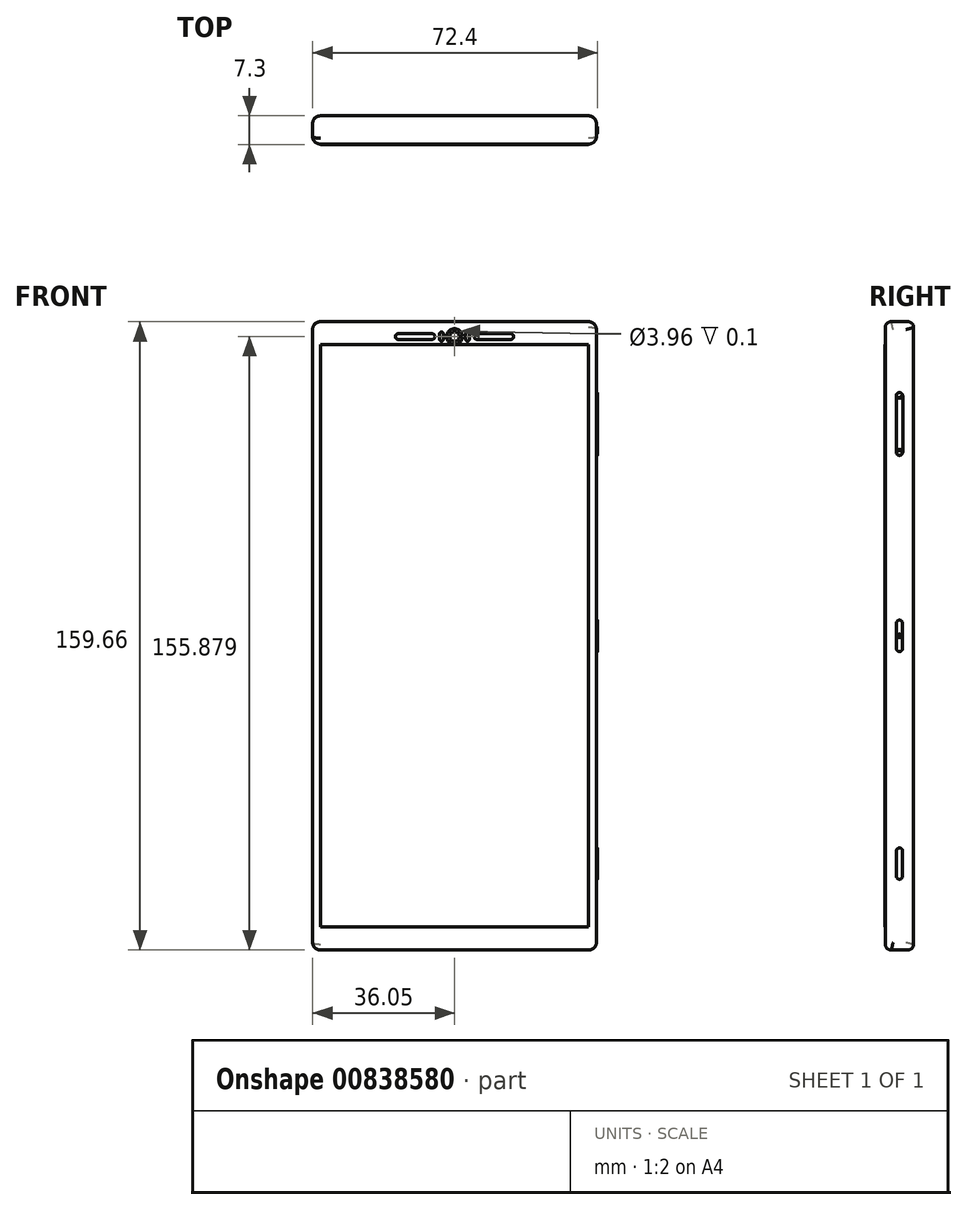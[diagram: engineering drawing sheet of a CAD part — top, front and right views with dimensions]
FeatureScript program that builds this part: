
annotation { "Feature Type Name" : "Feature", "Feature Type Description" : "" }
export const myFeature = defineFeature(function(context is Context, id is Id, definition is map)
    precondition{}
    {
        {
            var Q0;
            Q0=qCreatedBy(makeId("Front.planeOp"),FACE);
            var sketch = newSketch(context, id + "F0", { "sketchPlane" : qUnion([Q0])});
            skLineSegment(sketch, "E0.bottom", {"start": v(36.05, -79.83) * mm, "end": v(-36.05, -79.83) * mm});
            skLineSegment(sketch, "E0.top", {"start": v(36.05, 79.83) * mm, "end": v(-36.05, 79.83) * mm});
            skLineSegment(sketch, "E0.left", {"start": v(36.05, -79.83) * mm, "end": v(36.05, 79.83) * mm});
            skLineSegment(sketch, "E0.right", {"start": v(-36.05, -79.83) * mm, "end": v(-36.05, 79.83) * mm});
            skPoint(sketch, "E0.middle", {"position": v(0, 0) * mm});
            skSolve(sketch);
        }
        {
            var Q0;
            Q0=makeQuery(id+"F0.imprint","IMPRINT",FACE,{"disambiguationData":[TD([[makeQuery(id+"F0.imprint","IMPRINT",EDGE,{"derivedFrom":sQuery(id+"F0.wireOp",EDGE,"E0.bottom")}),-1.0]])]});
            extrude(context, id + "F1", {"entities" : qUnion([Q0]), "depth" : 7.2 * mm, "offsetDistance" : 25 * mm});
        }
        {
            var Q0;
            Q0=makeQuery(id+"F1.opExtrude","CAP_EDGE",EDGE,{"disambiguationData":[OSD([sQuery(id+"F0.wireOp",EDGE,"E0.bottom")])],"isStart":false});
            var Q1;
            Q1=makeQuery(id+"F1.opExtrude","CAP_EDGE",EDGE,{"disambiguationData":[OSD([sQuery(id+"F0.wireOp",EDGE,"E0.bottom")])],"isStart":true});
            var Q2;
            Q2=makeQuery(id+"F1.opExtrude","CAP_EDGE",EDGE,{"disambiguationData":[OSD([sQuery(id+"F0.wireOp",EDGE,"E0.top")])],"isStart":false});
            var Q3;
            Q3=makeQuery(id+"F1.opExtrude","CAP_EDGE",EDGE,{"disambiguationData":[OSD([sQuery(id+"F0.wireOp",EDGE,"E0.top")])],"isStart":true});
            fillet(context, id + "F2", {"entities" : qUnion([Q0, Q1, Q2, Q3]), "radius" : 1.5 * mm, "tangentPropagation" : true, "allowEdgeOverflow" : false});
        }
        {
            var Q0;
            Q0=makeQuery(id+"F1.opExtrude","CAP_EDGE",EDGE,{"disambiguationData":[OSD([sQuery(id+"F0.wireOp",EDGE,"E0.right")])],"isStart":false});
            var Q1;
            Q1=makeQuery(id+"F1.opExtrude","CAP_EDGE",EDGE,{"disambiguationData":[OSD([sQuery(id+"F0.wireOp",EDGE,"E0.left")])],"isStart":false});
            fillet(context, id + "F3", {"entities" : qUnion([Q0, Q1]), "radius" : 2 * mm, "tangentPropagation" : true, "allowEdgeOverflow" : false});
        }
        {
            var Q0;
            Q0=makeQuery(id+"F1.opExtrude","CAP_FACE",FACE,{"disambiguationData":[OSD([sQuery(id+"F0.wireOp",EDGE,"E0.bottom"),sQuery(id+"F0.wireOp",EDGE,"E0.top"),sQuery(id+"F0.wireOp",EDGE,"E0.left"),sQuery(id+"F0.wireOp",EDGE,"E0.right")])],"isStart":false});
            var sketch = newSketch(context, id + "F4", { "sketchPlane" : qUnion([Q0])});
            skLineSegment(sketch, "E1.bottom", {"start": v(34.05, -74) * mm, "end": v(-34.05, -74) * mm});
            skLineSegment(sketch, "E1.top", {"start": v(34.05, 74) * mm, "end": v(-34.05, 74) * mm});
            skLineSegment(sketch, "E1.left", {"start": v(34.05, -74) * mm, "end": v(34.05, 74) * mm});
            skLineSegment(sketch, "E1.right", {"start": v(-34.05, -74) * mm, "end": v(-34.05, 74) * mm});
            skPoint(sketch, "E1.middle", {"position": v(0, 0) * mm});
            skSolve(sketch);
        }
        {
            var Q0;
            {var subQ0=sQuery(id+"F4.wireOp",EDGE,"E1.top");Q0=makeQuery(id+"F4.imprint","IMPRINT",FACE,{"disambiguationData":[TD([[makeQuery(id+"F4.imprint","IMPRINT",EDGE,{"derivedFrom":subQ0}),-1.0]])]});}
            var sketch = newSketch(context, id + "F5", { "sketchPlane" : qUnion([Q0])});
            skCircle(sketch, "E2", {"center": v(0, 76.05) * mm, "radius": 1.98 * mm});
            skCircle(sketch, "E3", {"center": v(0, 76.05) * mm, "radius": 1.22 * mm});
            skLineSegment(sketch, "E4.bottom", {"start": v(15.02, 75.32) * mm, "end": v(5, 75.32) * mm});
            skLineSegment(sketch, "E4.top", {"start": v(15.02, 76.77) * mm, "end": v(5, 76.77) * mm});
            skLineSegment(sketch, "E4.left", {"start": v(15.02, 75.32) * mm, "end": v(15.02, 76.77) * mm});
            skLineSegment(sketch, "E4.right", {"start": v(5, 75.32) * mm, "end": v(5, 76.77) * mm});
            skLineSegment(sketch, "E5.bottom", {"start": v(-4.99, 75.32) * mm, "end": v(-15.03, 75.32) * mm});
            skLineSegment(sketch, "E5.top", {"start": v(-4.99, 76.77) * mm, "end": v(-15.03, 76.77) * mm});
            skLineSegment(sketch, "E5.left", {"start": v(-4.99, 75.32) * mm, "end": v(-4.99, 76.77) * mm});
            skLineSegment(sketch, "E5.right", {"start": v(-15.03, 75.32) * mm, "end": v(-15.03, 76.77) * mm});
            skLineSegment(sketch, "E6.bottom", {"start": v(3.8, 74.84) * mm, "end": v(2.83, 74.84) * mm});
            skLineSegment(sketch, "E6.top", {"start": v(3.8, 77.26) * mm, "end": v(2.83, 77.26) * mm});
            skLineSegment(sketch, "E6.left", {"start": v(3.8, 74.84) * mm, "end": v(3.8, 77.26) * mm});
            skLineSegment(sketch, "E6.right", {"start": v(2.83, 74.84) * mm, "end": v(2.83, 77.26) * mm});
            skLineSegment(sketch, "E7.bottom", {"start": v(-2.83, 74.84) * mm, "end": v(-3.8, 74.84) * mm});
            skLineSegment(sketch, "E7.top", {"start": v(-2.83, 77.26) * mm, "end": v(-3.8, 77.26) * mm});
            skLineSegment(sketch, "E7.left", {"start": v(-2.83, 74.84) * mm, "end": v(-2.83, 77.26) * mm});
            skLineSegment(sketch, "E7.right", {"start": v(-3.8, 74.84) * mm, "end": v(-3.8, 77.26) * mm});
            skSolve(sketch);
        }
        {
            var Q0;
            Q0=makeQuery(id+"F5.imprint","IMPRINT",FACE,{"disambiguationData":[TD([[makeQuery(id+"F5.imprint","IMPRINT",EDGE,{"derivedFrom":sQuery(id+"F5.wireOp",EDGE,"E5.bottom")}),-1.0]])]});
            var Q1;
            Q1=makeQuery(id+"F5.imprint","IMPRINT",FACE,{"disambiguationData":[TD([[makeQuery(id+"F5.imprint","IMPRINT",EDGE,{"derivedFrom":sQuery(id+"F5.wireOp",EDGE,"E4.bottom")}),-1.0]])]});
            var Q2;
            Q2=makeQuery(id+"F5.imprint","IMPRINT",FACE,{"disambiguationData":[TD([[makeQuery(id+"F5.imprint","IMPRINT",EDGE,{"derivedFrom":sQuery(id+"F5.wireOp",EDGE,"E6.bottom")}),-1.0]])]});
            var Q3;
            Q3=makeQuery(id+"F5.imprint","IMPRINT",FACE,{"disambiguationData":[TD([[makeQuery(id+"F5.imprint","IMPRINT",EDGE,{"derivedFrom":sQuery(id+"F5.wireOp",EDGE,"E7.bottom")}),-1.0]])]});
            var Q4;
            Q4=makeQuery(id+"F5.imprint","IMPRINT",FACE,{"disambiguationData":[TD([[makeQuery(id+"F5.imprint","IMPRINT",EDGE,{"derivedFrom":sQuery(id+"F5.wireOp",EDGE,"E2")}),1.0]])]});
            var Q5;
            Q5=sQuery(id+"F5.wireOp",EDGE,"E5.right");
            var Q6;
            Q6=sQuery(id+"F5.wireOp",EDGE,"E5.top");
            var Q7;
            Q7=sQuery(id+"F5.wireOp",EDGE,"E5.bottom");
            var Q8;
            Q8=sQuery(id+"F5.wireOp",EDGE,"E5.left");
            var Q9;
            Q9=sQuery(id+"F5.wireOp",EDGE,"E4.top");
            var Q10;
            Q10=sQuery(id+"F5.wireOp",EDGE,"E4.bottom");
            var Q11;
            Q11=sQuery(id+"F5.wireOp",EDGE,"E4.right");
            var Q12;
            Q12=sQuery(id+"F5.wireOp",EDGE,"E4.left");
            var Q13;
            Q13=sQuery(id+"F5.wireOp",EDGE,"E7.right");
            var Q14;
            Q14=sQuery(id+"F5.wireOp",EDGE,"E7.top");
            var Q15;
            Q15=sQuery(id+"F5.wireOp",EDGE,"E7.left");
            var Q16;
            Q16=sQuery(id+"F5.wireOp",EDGE,"E7.bottom");
            var Q17;
            Q17=sQuery(id+"F5.wireOp",EDGE,"E2");
            var Q18;
            Q18=sQuery(id+"F5.wireOp",EDGE,"E3");
            var Q19;
            Q19=sQuery(id+"F5.wireOp",EDGE,"E6.right");
            var Q20;
            Q20=sQuery(id+"F5.wireOp",EDGE,"E6.top");
            var Q21;
            Q21=sQuery(id+"F5.wireOp",EDGE,"E6.left");
            var Q22;
            Q22=sQuery(id+"F5.wireOp",EDGE,"E6.bottom");
            extrude(context, id + "F6", {"entities" : qUnion([Q0, Q1, Q2, Q3, Q4]), "operationType" : NewBodyOperationType.REMOVE, "surfaceEntities" : qUnion([Q5, Q6, Q7, Q8, Q9, Q10, Q11, Q12, Q13, Q14, Q15, Q16, Q17, Q18, Q19, Q20, Q21, Q22]), "oppositeDirection" : true, "depth" : .1 * mm, "offsetDistance" : 25 * mm});
        }
        {
            var Q0;
            Q0=makeQuery(id+"F6.boolean.opBoolean","COPY",EDGE,{"derivedFrom":makeQuery(id+"F6.opExtrude","SWEPT_EDGE",EDGE,{"disambiguationData":[OSD([sQuery(id+"F5.wireOp",EDGE,"E5.bottom"),sQuery(id+"F5.wireOp",EDGE,"E5.left")])]})});
            var Q1;
            Q1=makeQuery(id+"F6.boolean.opBoolean","COPY",EDGE,{"derivedFrom":makeQuery(id+"F6.opExtrude","SWEPT_EDGE",EDGE,{"disambiguationData":[OSD([sQuery(id+"F5.wireOp",EDGE,"E5.top"),sQuery(id+"F5.wireOp",EDGE,"E5.left")])]})});
            var Q2;
            Q2=makeQuery(id+"F6.boolean.opBoolean","COPY",EDGE,{"derivedFrom":makeQuery(id+"F6.opExtrude","SWEPT_EDGE",EDGE,{"disambiguationData":[OSD([sQuery(id+"F5.wireOp",EDGE,"E5.bottom"),sQuery(id+"F5.wireOp",EDGE,"E5.right")])]})});
            var Q3;
            Q3=makeQuery(id+"F6.boolean.opBoolean","COPY",EDGE,{"derivedFrom":makeQuery(id+"F6.opExtrude","SWEPT_EDGE",EDGE,{"disambiguationData":[OSD([sQuery(id+"F5.wireOp",EDGE,"E5.top"),sQuery(id+"F5.wireOp",EDGE,"E5.right")])]})});
            var Q4;
            Q4=makeQuery(id+"F6.boolean.opBoolean","COPY",EDGE,{"derivedFrom":makeQuery(id+"F6.opExtrude","SWEPT_EDGE",EDGE,{"disambiguationData":[OSD([sQuery(id+"F5.wireOp",EDGE,"E4.bottom"),sQuery(id+"F5.wireOp",EDGE,"E4.right")])]})});
            var Q5;
            Q5=makeQuery(id+"F6.boolean.opBoolean","COPY",EDGE,{"derivedFrom":makeQuery(id+"F6.opExtrude","SWEPT_EDGE",EDGE,{"disambiguationData":[OSD([sQuery(id+"F5.wireOp",EDGE,"E4.top"),sQuery(id+"F5.wireOp",EDGE,"E4.right")])]})});
            var Q6;
            Q6=makeQuery(id+"F6.boolean.opBoolean","COPY",EDGE,{"derivedFrom":makeQuery(id+"F6.opExtrude","SWEPT_EDGE",EDGE,{"disambiguationData":[OSD([sQuery(id+"F5.wireOp",EDGE,"E4.bottom"),sQuery(id+"F5.wireOp",EDGE,"E4.left")])]})});
            var Q7;
            Q7=makeQuery(id+"F6.boolean.opBoolean","COPY",EDGE,{"derivedFrom":makeQuery(id+"F6.opExtrude","SWEPT_EDGE",EDGE,{"disambiguationData":[OSD([sQuery(id+"F5.wireOp",EDGE,"E4.top"),sQuery(id+"F5.wireOp",EDGE,"E4.left")])]})});
            fillet(context, id + "F7", {"entities" : qUnion([Q0, Q1, Q2, Q3, Q4, Q5, Q6, Q7]), "radius" : .7 * mm, "tangentPropagation" : true, "allowEdgeOverflow" : false});
        }
        {
            var Q0;
            Q0=makeQuery(id+"F6.boolean.opBoolean","COPY",EDGE,{"derivedFrom":makeQuery(id+"F6.opExtrude","SWEPT_EDGE",EDGE,{"disambiguationData":[OSD([sQuery(id+"F5.wireOp",EDGE,"E7.bottom"),sQuery(id+"F5.wireOp",EDGE,"E7.left")])]})});
            var Q1;
            Q1=makeQuery(id+"F6.boolean.opBoolean","COPY",EDGE,{"derivedFrom":makeQuery(id+"F6.opExtrude","SWEPT_EDGE",EDGE,{"disambiguationData":[OSD([sQuery(id+"F5.wireOp",EDGE,"E7.bottom"),sQuery(id+"F5.wireOp",EDGE,"E7.right")])]})});
            var Q2;
            Q2=makeQuery(id+"F6.boolean.opBoolean","COPY",EDGE,{"derivedFrom":makeQuery(id+"F6.opExtrude","SWEPT_EDGE",EDGE,{"disambiguationData":[OSD([sQuery(id+"F5.wireOp",EDGE,"E7.top"),sQuery(id+"F5.wireOp",EDGE,"E7.right")])]})});
            var Q3;
            Q3=makeQuery(id+"F6.boolean.opBoolean","COPY",EDGE,{"derivedFrom":makeQuery(id+"F6.opExtrude","SWEPT_EDGE",EDGE,{"disambiguationData":[OSD([sQuery(id+"F5.wireOp",EDGE,"E7.top"),sQuery(id+"F5.wireOp",EDGE,"E7.left")])]})});
            var Q4;
            Q4=makeQuery(id+"F6.boolean.opBoolean","COPY",EDGE,{"derivedFrom":makeQuery(id+"F6.opExtrude","SWEPT_EDGE",EDGE,{"disambiguationData":[OSD([sQuery(id+"F5.wireOp",EDGE,"E6.top"),sQuery(id+"F5.wireOp",EDGE,"E6.left")])]})});
            var Q5;
            Q5=makeQuery(id+"F6.boolean.opBoolean","COPY",EDGE,{"derivedFrom":makeQuery(id+"F6.opExtrude","SWEPT_EDGE",EDGE,{"disambiguationData":[OSD([sQuery(id+"F5.wireOp",EDGE,"E6.bottom"),sQuery(id+"F5.wireOp",EDGE,"E6.left")])]})});
            var Q6;
            Q6=makeQuery(id+"F6.boolean.opBoolean","COPY",EDGE,{"derivedFrom":makeQuery(id+"F6.opExtrude","SWEPT_EDGE",EDGE,{"disambiguationData":[OSD([sQuery(id+"F5.wireOp",EDGE,"E6.bottom"),sQuery(id+"F5.wireOp",EDGE,"E6.right")])]})});
            var Q7;
            Q7=makeQuery(id+"F6.boolean.opBoolean","COPY",EDGE,{"derivedFrom":makeQuery(id+"F6.opExtrude","SWEPT_EDGE",EDGE,{"disambiguationData":[OSD([sQuery(id+"F5.wireOp",EDGE,"E6.top"),sQuery(id+"F5.wireOp",EDGE,"E6.right")])]})});
            fillet(context, id + "F8", {"entities" : qUnion([Q0, Q1, Q2, Q3, Q4, Q5, Q6, Q7]), "radius" : .6 * mm, "tangentPropagation" : true, "allowEdgeOverflow" : false});
        }
        {
            var Q0;
            Q0=makeQuery(id+"F4.imprint","IMPRINT",FACE,{"disambiguationData":[TD([[makeQuery(id+"F4.imprint","IMPRINT",EDGE,{"derivedFrom":sQuery(id+"F4.wireOp",EDGE,"E1.bottom")}),-1.0]])]});
            extrude(context, id + "F9", {"entities" : qUnion([Q0]), "operationType" : NewBodyOperationType.ADD, "depth" : .1 * mm, "offsetDistance" : 25 * mm});
        }
        {
            var Q0;
            Q0=makeQuery(id+"F1.opExtrude","SWEPT_FACE",FACE,{"disambiguationData":[OSD([sQuery(id+"F0.wireOp",EDGE,"E0.left")])]});
            var sketch = newSketch(context, id + "F10", { "sketchPlane" : qUnion([Q0])});
            skLineSegment(sketch, "E8.bottom", {"start": v(-2.82, -4) * mm, "end": v(-4.38, -4) * mm});
            skLineSegment(sketch, "E8.top", {"start": v(-2.82, 4) * mm, "end": v(-4.38, 4) * mm});
            skLineSegment(sketch, "E8.left", {"start": v(-2.82, -4) * mm, "end": v(-2.82, 4) * mm});
            skLineSegment(sketch, "E8.right", {"start": v(-4.38, -4) * mm, "end": v(-4.38, 4) * mm});
            skLineSegment(sketch, "E9.bottom", {"start": v(-4.38, -61.85) * mm, "end": v(-2.82, -61.85) * mm});
            skLineSegment(sketch, "E9.top", {"start": v(-4.38, -53.89) * mm, "end": v(-2.82, -53.89) * mm});
            skLineSegment(sketch, "E9.left", {"start": v(-4.38, -61.85) * mm, "end": v(-4.38, -53.89) * mm});
            skLineSegment(sketch, "E9.right", {"start": v(-2.82, -61.85) * mm, "end": v(-2.82, -53.89) * mm});
            skLineSegment(sketch, "E10.bottom", {"start": v(-2.78, 61.8) * mm, "end": v(-4.42, 61.8) * mm});
            skLineSegment(sketch, "E10.top", {"start": v(-2.78, 45.87) * mm, "end": v(-4.42, 45.87) * mm});
            skLineSegment(sketch, "E10.left", {"start": v(-2.78, 61.8) * mm, "end": v(-2.78, 45.87) * mm});
            skLineSegment(sketch, "E10.right", {"start": v(-4.42, 61.8) * mm, "end": v(-4.42, 45.87) * mm});
            skSolve(sketch);
        }
        {
            var Q0;
            Q0=makeQuery(id+"F10.imprint","IMPRINT",FACE,{"disambiguationData":[TD([[makeQuery(id+"F10.imprint","IMPRINT",EDGE,{"derivedFrom":sQuery(id+"F10.wireOp",EDGE,"E8.bottom")}),-1.0]])]});
            var Q1;
            Q1=makeQuery(id+"F10.imprint","IMPRINT",FACE,{"disambiguationData":[TD([[makeQuery(id+"F10.imprint","IMPRINT",EDGE,{"derivedFrom":sQuery(id+"F10.wireOp",EDGE,"E9.bottom")}),1.0]])]});
            var Q2;
            Q2=makeQuery(id+"F10.imprint","IMPRINT",FACE,{"disambiguationData":[TD([[makeQuery(id+"F10.imprint","IMPRINT",EDGE,{"derivedFrom":sQuery(id+"F10.wireOp",EDGE,"E10.bottom")}),1.0]])]});
            extrude(context, id + "F11", {"entities" : qUnion([Q0, Q1, Q2]), "operationType" : NewBodyOperationType.ADD, "depth" : .3 * mm, "offsetDistance" : 25 * mm});
        }
        {
            var Q0;
            Q0=makeQuery(id+"F11.opExtrude","CAP_FACE",FACE,{"disambiguationData":[OSD([sQuery(id+"F10.wireOp",EDGE,"E8.bottom"),sQuery(id+"F10.wireOp",EDGE,"E8.top"),sQuery(id+"F10.wireOp",EDGE,"E8.left"),sQuery(id+"F10.wireOp",EDGE,"E8.right")])],"isStart":false});
            var sketch = newSketch(context, id + "F12", { "sketchPlane" : qUnion([Q0])});
            skCircle(sketch, "E11", {"center": v(-3.6, 0) * mm, "radius": 0.3 * mm});
            skCircle(sketch, "E12", {"center": v(-3.6, 0) * mm, "radius": 0.44 * mm});
            skLineSegment(sketch, "E13.bottom", {"start": v(-3.68, -0.07) * mm, "end": v(-4.24, -0.07) * mm});
            skLineSegment(sketch, "E13.top", {"start": v(-3.68, 0.07) * mm, "end": v(-4.24, 0.07) * mm});
            skLineSegment(sketch, "E13.left", {"start": v(-3.68, -0.07) * mm, "end": v(-3.68, 0.07) * mm});
            skLineSegment(sketch, "E13.right", {"start": v(-4.24, -0.07) * mm, "end": v(-4.24, 0.07) * mm});
            skPoint(sketch, "E13.middle", {"position": v(-3.96, 0) * mm});
            skLineSegment(sketch, "E14", {"start": v(-4.03, 0.07) * mm, "end": v(-3.9, 0.07) * mm});
            skLineSegment(sketch, "E15", {"start": v(-4.03, -0.07) * mm, "end": v(-3.9, -0.07) * mm});
            skLineSegment(sketch, "E16", {"start": v(-3.88, 0.1) * mm, "end": v(-4.02, 0.1) * mm});
            skLineSegment(sketch, "E17", {"start": v(-3.88, -0.1) * mm, "end": v(-4.02, -0.1) * mm});
            skSolve(sketch);
        }
        {
            var Q0;
            {var subQ0=sQuery(id+"F12.wireOp",EDGE,"E16");Q0=makeQuery(id+"F12.imprint","IMPRINT",FACE,{"disambiguationData":[TD([[makeQuery(id+"F12.imprint","IMPRINT",EDGE,{"derivedFrom":subQ0}),-1.0]])]});}
            var Q1;
            {var subQ5=sQuery(id+"F12.wireOp",EDGE,"E13.left");Q1=makeQuery(id+"F12.imprint","IMPRINT",FACE,{"disambiguationData":[TD([[makeQuery(id+"F12.imprint","IMPRINT",EDGE,{"derivedFrom":subQ5}),1.0]])]});}
            var Q2;
            {var subQ0=sQuery(id+"F12.wireOp",EDGE,"E14");Q2=makeQuery(id+"F12.imprint","IMPRINT",FACE,{"disambiguationData":[TD([[makeQuery(id+"F12.imprint","IMPRINT",EDGE,{"derivedFrom":subQ0}),-1.0]])]});}
            var Q3;
            {var subQ5=sQuery(id+"F12.wireOp",EDGE,"E13.right");Q3=makeQuery(id+"F12.imprint","IMPRINT",FACE,{"disambiguationData":[TD([[makeQuery(id+"F12.imprint","IMPRINT",EDGE,{"derivedFrom":subQ5}),-1.0]])]});}
            extrude(context, id + "F13", {"entities" : qUnion([Q0, Q1, Q2, Q3]), "operationType" : NewBodyOperationType.REMOVE, "oppositeDirection" : true, "depth" : .2 * mm, "offsetDistance" : 25 * mm});
        }
        {
            var Q0;
            Q0=makeQuery(id+"F11.opExtrude","SWEPT_EDGE",EDGE,{"disambiguationData":[OSD([sQuery(id+"F10.wireOp",EDGE,"E8.top"),sQuery(id+"F10.wireOp",EDGE,"E8.right")])]});
            var Q1;
            Q1=makeQuery(id+"F11.opExtrude","SWEPT_EDGE",EDGE,{"disambiguationData":[OSD([sQuery(id+"F10.wireOp",EDGE,"E8.top"),sQuery(id+"F10.wireOp",EDGE,"E8.left")])]});
            var Q2;
            Q2=makeQuery(id+"F11.opExtrude","SWEPT_EDGE",EDGE,{"disambiguationData":[OSD([sQuery(id+"F10.wireOp",EDGE,"E8.bottom"),sQuery(id+"F10.wireOp",EDGE,"E8.right")])]});
            var Q3;
            Q3=makeQuery(id+"F11.opExtrude","SWEPT_EDGE",EDGE,{"disambiguationData":[OSD([sQuery(id+"F10.wireOp",EDGE,"E8.bottom"),sQuery(id+"F10.wireOp",EDGE,"E8.left")])]});
            var Q4;
            Q4=makeQuery(id+"F11.opExtrude","SWEPT_EDGE",EDGE,{"disambiguationData":[OSD([sQuery(id+"F10.wireOp",EDGE,"E9.bottom"),sQuery(id+"F10.wireOp",EDGE,"E9.right")])]});
            var Q5;
            Q5=makeQuery(id+"F11.opExtrude","SWEPT_EDGE",EDGE,{"disambiguationData":[OSD([sQuery(id+"F10.wireOp",EDGE,"E9.bottom"),sQuery(id+"F10.wireOp",EDGE,"E9.left")])]});
            var Q6;
            Q6=makeQuery(id+"F11.opExtrude","SWEPT_EDGE",EDGE,{"disambiguationData":[OSD([sQuery(id+"F10.wireOp",EDGE,"E9.top"),sQuery(id+"F10.wireOp",EDGE,"E9.right")])]});
            var Q7;
            Q7=makeQuery(id+"F11.opExtrude","SWEPT_EDGE",EDGE,{"disambiguationData":[OSD([sQuery(id+"F10.wireOp",EDGE,"E9.top"),sQuery(id+"F10.wireOp",EDGE,"E9.left")])]});
            var Q8;
            Q8=makeQuery(id+"F11.opExtrude","SWEPT_EDGE",EDGE,{"disambiguationData":[OSD([sQuery(id+"F10.wireOp",EDGE,"E10.top"),sQuery(id+"F10.wireOp",EDGE,"E10.left")])]});
            var Q9;
            Q9=makeQuery(id+"F11.opExtrude","SWEPT_EDGE",EDGE,{"disambiguationData":[OSD([sQuery(id+"F10.wireOp",EDGE,"E10.top"),sQuery(id+"F10.wireOp",EDGE,"E10.right")])]});
            var Q10;
            Q10=makeQuery(id+"F11.opExtrude","SWEPT_EDGE",EDGE,{"disambiguationData":[OSD([sQuery(id+"F10.wireOp",EDGE,"E10.bottom"),sQuery(id+"F10.wireOp",EDGE,"E10.left")])]});
            var Q11;
            Q11=makeQuery(id+"F11.opExtrude","SWEPT_EDGE",EDGE,{"disambiguationData":[OSD([sQuery(id+"F10.wireOp",EDGE,"E10.bottom"),sQuery(id+"F10.wireOp",EDGE,"E10.right")])]});
            fillet(context, id + "F14", {"entities" : qUnion([Q0, Q1, Q2, Q3, Q4, Q5, Q6, Q7, Q8, Q9, Q10, Q11]), "radius" : .8 * mm, "tangentPropagation" : true, "allowEdgeOverflow" : false});
        }
        {
            var Q0;
            Q0=makeQuery(id+"F11.opExtrude","CAP_FACE",FACE,{"disambiguationData":[OSD([sQuery(id+"F10.wireOp",EDGE,"E10.bottom"),sQuery(id+"F10.wireOp",EDGE,"E10.top"),sQuery(id+"F10.wireOp",EDGE,"E10.left"),sQuery(id+"F10.wireOp",EDGE,"E10.right")])],"isStart":false});
            var sketch = newSketch(context, id + "F15", { "sketchPlane" : qUnion([Q0])});
            skLineSegment(sketch, "E18.0", {"start": v(-3.58, 61) * mm, "end": v(-3.24, 60.4) * mm});
            skLineSegment(sketch, "E18.1", {"start": v(-3.24, 60.4) * mm, "end": v(-3.92, 60.4) * mm});
            skLineSegment(sketch, "E18.2", {"start": v(-3.92, 60.4) * mm, "end": v(-3.58, 61) * mm});
            skLineSegment(sketch, "E19.0", {"start": v(-3.62, 46.67) * mm, "end": v(-3.97, 47.28) * mm});
            skLineSegment(sketch, "E19.1", {"start": v(-3.97, 47.28) * mm, "end": v(-3.26, 47.28) * mm});
            skLineSegment(sketch, "E19.2", {"start": v(-3.26, 47.28) * mm, "end": v(-3.62, 46.67) * mm});
            skSolve(sketch);
        }
        {
            var Q0;
            Q0=makeQuery(id+"F15.imprint","IMPRINT",FACE,{"disambiguationData":[TD([[makeQuery(id+"F15.imprint","IMPRINT",EDGE,{"derivedFrom":sQuery(id+"F15.wireOp",EDGE,"E18.0")}),-1.0]])]});
            var Q1;
            Q1=makeQuery(id+"F15.imprint","IMPRINT",FACE,{"disambiguationData":[TD([[makeQuery(id+"F15.imprint","IMPRINT",EDGE,{"derivedFrom":sQuery(id+"F15.wireOp",EDGE,"E19.0")}),-1.0]])]});
            extrude(context, id + "F16", {"entities" : qUnion([Q0, Q1]), "operationType" : NewBodyOperationType.REMOVE, "oppositeDirection" : true, "depth" : .2 * mm, "offsetDistance" : 25 * mm});
        }
    });
